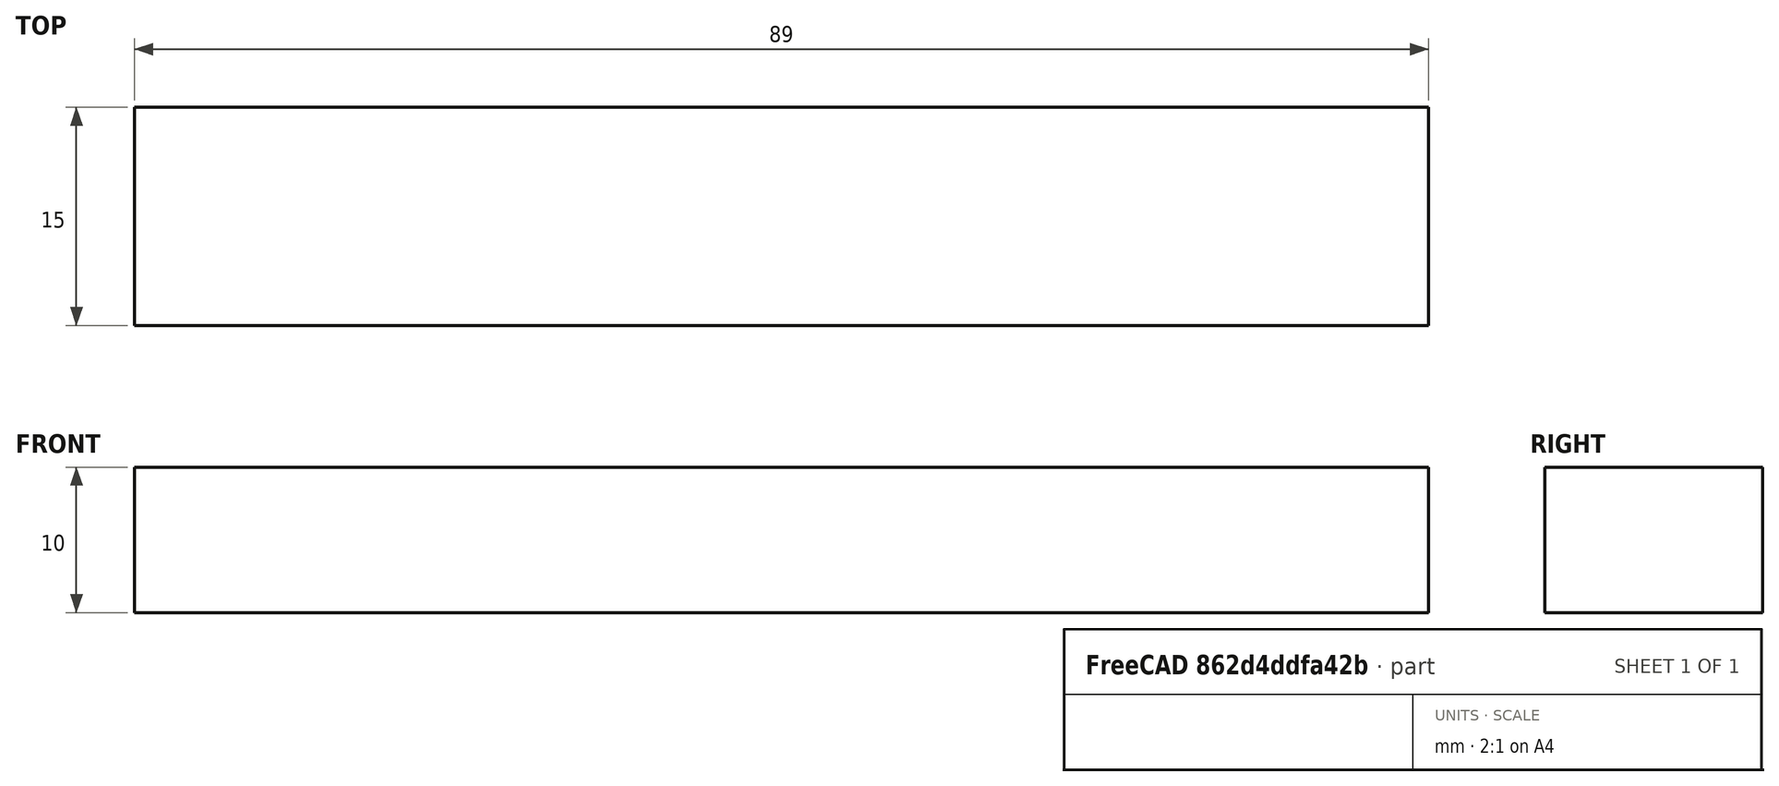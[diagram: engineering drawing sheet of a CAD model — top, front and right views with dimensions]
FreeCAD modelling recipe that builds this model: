
FCSTD DOCUMENT  (FreeCAD 0.18.1R)
Label: LTE-antenna
License: All rights reserved
LicenseURL: http://en.wikipedia.org/wiki/All_rights_reserved
objects: Sketcher::SketchObject×1, PartDesign::Pad×1, PartDesign::Body×1
note: 4 computed .brp shape members not serialized (recipe doc carries the construction recipe); baked Part::Feature solids carry a one-line shape summary decoded from their .brp

FEATURE [Sketcher::SketchObject] Sketch
  MapMode = 5
  Support = -> [XY_Plane]
  sketch-geometry (4):
    g0: LineSegment StartX=-89 StartY=15 StartZ=0 EndX=0 EndY=15 EndZ=0
    g1: LineSegment StartX=0 StartY=15 StartZ=0 EndX=0 EndY=0 EndZ=0
    g2: LineSegment StartX=0 StartY=0 StartZ=0 EndX=-89 EndY=0 EndZ=0
    g3: LineSegment StartX=-89 StartY=0 StartZ=0 EndX=-89 EndY=15 EndZ=0
  constraints (11):
    c: Coincident(g0,g1)
    c: Coincident(g1,g2)
    c: Coincident(g2,g3)
    c: Coincident(g3,g0)
    c: Horizontal(g0)
    c: Horizontal(g2)
    c: Vertical(g1)
    c: Vertical(g3)
    c: Distance(g0) = 89
    c: Distance(g3) = 15
    c: Coincident(g-1,g1)
FEATURE [PartDesign::Pad] Pad
  Length = 1.3
  Length2 = 100
  Profile = -> Sketch
  Type = 0
FEATURE [PartDesign::Body] Body
  Group = -> [Sketch,Pad]
  Origin = -> Origin
  Tip = -> Pad
